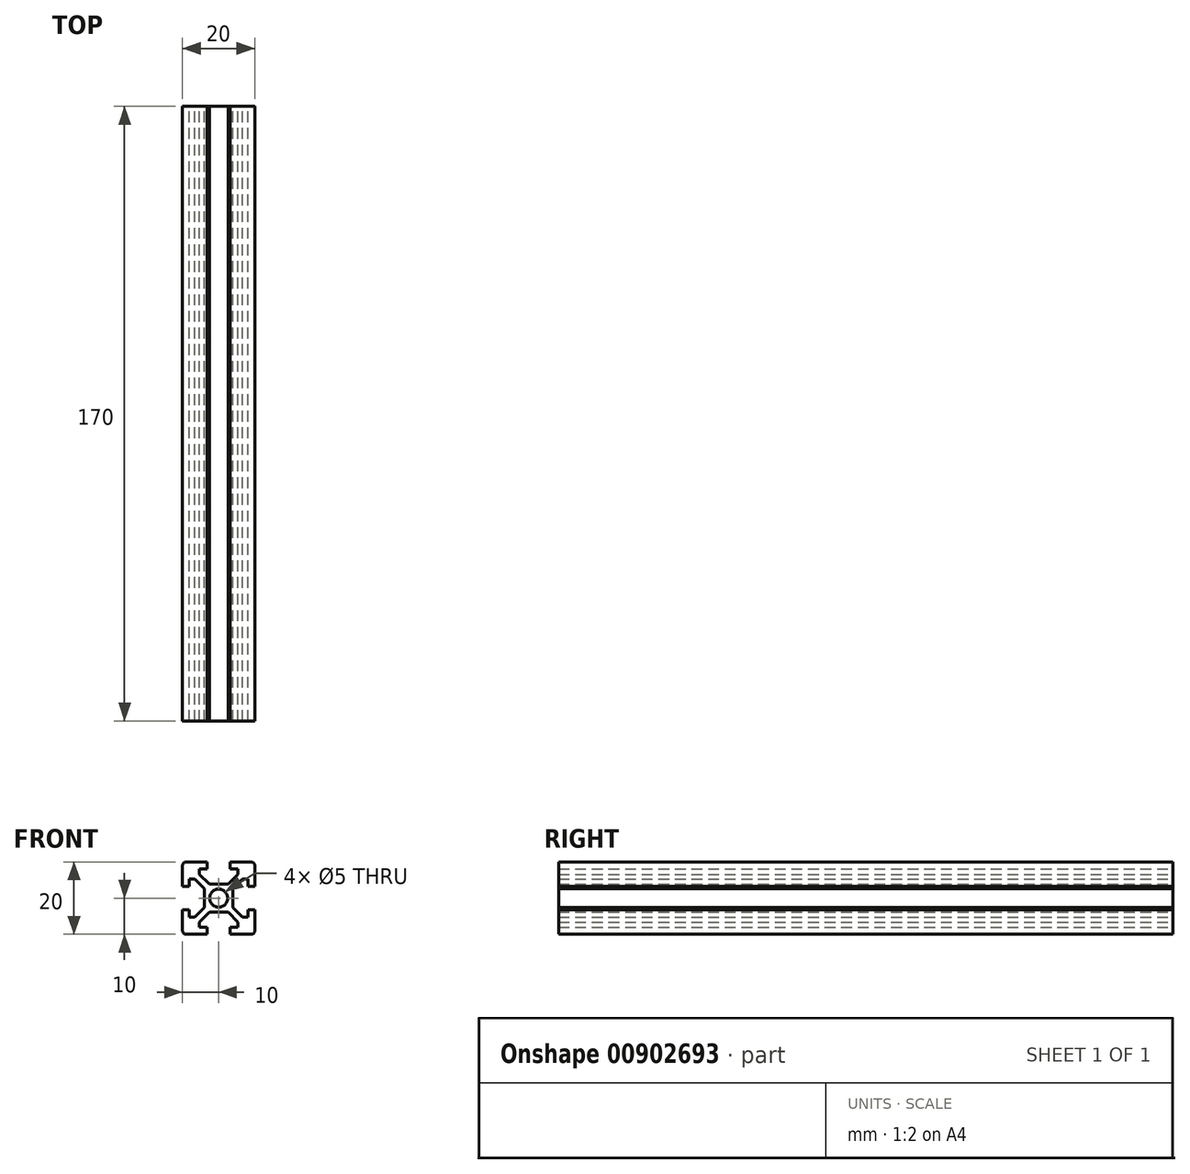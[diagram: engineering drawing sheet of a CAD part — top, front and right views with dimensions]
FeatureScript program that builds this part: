
annotation { "Feature Type Name" : "Feature", "Feature Type Description" : "" }
export const myFeature = defineFeature(function(context is Context, id is Id, definition is map)
    precondition{}
    {
        {
            var Q0;
            Q0=qCreatedBy(makeId("Front.planeOp"),FACE);
            var sketch = newSketch(context, id + "F0", { "sketchPlane" : qUnion([Q0])});
            skLineSegment(sketch, "E0", {"start": v(3.2, 10) * mm, "end": v(9, 10) * mm});
            skLineSegment(sketch, "E1", {"start": v(10, 9) * mm, "end": v(10, 3.2) * mm});
            skLineSegment(sketch, "E2", {"start": v(10, 3.2) * mm, "end": v(8.1, 3.2) * mm});
            skLineSegment(sketch, "E3", {"start": v(8.1, 3.2) * mm, "end": v(8.1, 5.3) * mm});
            skLineSegment(sketch, "E4", {"start": v(8.1, 5.3) * mm, "end": v(6.6, 5.3) * mm});
            skLineSegment(sketch, "E5", {"start": v(5.3, 6.6) * mm, "end": v(5.3, 8.1) * mm});
            skLineSegment(sketch, "E6", {"start": v(5.3, 8.1) * mm, "end": v(3.2, 8.1) * mm});
            skLineSegment(sketch, "E7", {"start": v(3.2, 8.1) * mm, "end": v(3.2, 10) * mm});
            skArc(sketch, "E8", {"start": v(2.5, 0) * mm, "mid": v(1.77, 1.77) * mm, "end": v(0, 2.5) * mm});
            skLineSegment(sketch, "E9", {"start": v(0, 2.5) * mm, "end": v(0, 3.9) * mm});
            skLineSegment(sketch, "E10", {"start": v(0, 3.9) * mm, "end": v(2.6, 3.9) * mm});
            skLineSegment(sketch, "E11", {"start": v(2.6, 3.9) * mm, "end": v(5.3, 6.6) * mm});
            skLineSegment(sketch, "E12", {"start": v(6.6, 5.3) * mm, "end": v(3.9, 2.6) * mm});
            skLineSegment(sketch, "E13", {"start": v(3.9, 2.6) * mm, "end": v(3.9, 0) * mm});
            skLineSegment(sketch, "E14", {"start": v(3.9, 0) * mm, "end": v(2.5, 0) * mm});
            skPoint(sketch, "E15.visualSharp", {"position": v(10, 10) * mm});
            skArc(sketch, "E15.filletArc", {"start": v(10, 9) * mm, "mid": v(9.7, 9.7) * mm, "end": v(9, 10) * mm});
            skArc(sketch, "E16.1.0", {"start": v(0, 2.5) * mm, "mid": v(-1.77, 1.77) * mm, "end": v(-2.5, 0) * mm});
            skLineSegment(sketch, "E16.1.1", {"start": v(-5.3, 8.1) * mm, "end": v(-5.3, 6.6) * mm});
            skLineSegment(sketch, "E16.1.2", {"start": v(-5.3, 6.6) * mm, "end": v(-2.6, 3.9) * mm});
            skLineSegment(sketch, "E16.1.3", {"start": v(0, 3.9) * mm, "end": v(0, 2.5) * mm});
            skLineSegment(sketch, "E16.1.4", {"start": v(-3.2, 8.1) * mm, "end": v(-5.3, 8.1) * mm});
            skLineSegment(sketch, "E16.1.5", {"start": v(-2.6, 3.9) * mm, "end": v(0, 3.9) * mm});
            skLineSegment(sketch, "E16.1.6", {"start": v(-3.2, 10) * mm, "end": v(-3.2, 8.1) * mm});
            skLineSegment(sketch, "E16.1.7", {"start": v(-10, 3.2) * mm, "end": v(-10, 9) * mm});
            skLineSegment(sketch, "E16.1.8", {"start": v(-3.9, 0) * mm, "end": v(-3.9, 2.6) * mm});
            skLineSegment(sketch, "E16.1.9", {"start": v(-3.9, 2.6) * mm, "end": v(-6.6, 5.3) * mm});
            skLineSegment(sketch, "E16.1.10", {"start": v(-2.5, 0) * mm, "end": v(-3.9, 0) * mm});
            skLineSegment(sketch, "E16.1.11", {"start": v(-6.6, 5.3) * mm, "end": v(-8.1, 5.3) * mm});
            skLineSegment(sketch, "E16.1.12", {"start": v(-9, 10) * mm, "end": v(-3.2, 10) * mm});
            skLineSegment(sketch, "E16.1.13", {"start": v(-8.1, 5.3) * mm, "end": v(-8.1, 3.2) * mm});
            skLineSegment(sketch, "E16.1.14", {"start": v(-8.1, 3.2) * mm, "end": v(-10, 3.2) * mm});
            skPoint(sketch, "E16.1.15", {"position": v(-10, 10) * mm});
            skArc(sketch, "E16.1.16", {"start": v(-9, 10) * mm, "mid": v(-9.7, 9.7) * mm, "end": v(-10, 9) * mm});
            skArc(sketch, "E16.2.0", {"start": v(-2.5, 0) * mm, "mid": v(-1.77, -1.77) * mm, "end": v(0, -2.5) * mm});
            skLineSegment(sketch, "E16.2.1", {"start": v(-8.1, -5.3) * mm, "end": v(-6.6, -5.3) * mm});
            skLineSegment(sketch, "E16.2.2", {"start": v(-6.6, -5.3) * mm, "end": v(-3.9, -2.6) * mm});
            skLineSegment(sketch, "E16.2.3", {"start": v(-3.9, 0) * mm, "end": v(-2.5, 0) * mm});
            skLineSegment(sketch, "E16.2.4", {"start": v(-8.1, -3.2) * mm, "end": v(-8.1, -5.3) * mm});
            skLineSegment(sketch, "E16.2.5", {"start": v(-3.9, -2.6) * mm, "end": v(-3.9, 0) * mm});
            skLineSegment(sketch, "E16.2.6", {"start": v(-10, -3.2) * mm, "end": v(-8.1, -3.2) * mm});
            skLineSegment(sketch, "E16.2.7", {"start": v(-3.2, -10) * mm, "end": v(-9, -10) * mm});
            skLineSegment(sketch, "E16.2.8", {"start": v(0, -3.9) * mm, "end": v(-2.6, -3.9) * mm});
            skLineSegment(sketch, "E16.2.9", {"start": v(-2.6, -3.9) * mm, "end": v(-5.3, -6.6) * mm});
            skLineSegment(sketch, "E16.2.10", {"start": v(0, -2.5) * mm, "end": v(0, -3.9) * mm});
            skLineSegment(sketch, "E16.2.11", {"start": v(-5.3, -6.6) * mm, "end": v(-5.3, -8.1) * mm});
            skLineSegment(sketch, "E16.2.12", {"start": v(-10, -9) * mm, "end": v(-10, -3.2) * mm});
            skLineSegment(sketch, "E16.2.13", {"start": v(-5.3, -8.1) * mm, "end": v(-3.2, -8.1) * mm});
            skLineSegment(sketch, "E16.2.14", {"start": v(-3.2, -8.1) * mm, "end": v(-3.2, -10) * mm});
            skPoint(sketch, "E16.2.15", {"position": v(-10, -10) * mm});
            skArc(sketch, "E16.2.16", {"start": v(-10, -9) * mm, "mid": v(-9.7, -9.7) * mm, "end": v(-9, -10) * mm});
            skArc(sketch, "E16.3.0", {"start": v(0, -2.5) * mm, "mid": v(1.77, -1.77) * mm, "end": v(2.5, 0) * mm});
            skLineSegment(sketch, "E16.3.1", {"start": v(5.3, -8.1) * mm, "end": v(5.3, -6.6) * mm});
            skLineSegment(sketch, "E16.3.2", {"start": v(5.3, -6.6) * mm, "end": v(2.6, -3.9) * mm});
            skLineSegment(sketch, "E16.3.3", {"start": v(0, -3.9) * mm, "end": v(0, -2.5) * mm});
            skLineSegment(sketch, "E16.3.4", {"start": v(3.2, -8.1) * mm, "end": v(5.3, -8.1) * mm});
            skLineSegment(sketch, "E16.3.5", {"start": v(2.6, -3.9) * mm, "end": v(0, -3.9) * mm});
            skLineSegment(sketch, "E16.3.6", {"start": v(3.2, -10) * mm, "end": v(3.2, -8.1) * mm});
            skLineSegment(sketch, "E16.3.7", {"start": v(10, -3.2) * mm, "end": v(10, -9) * mm});
            skLineSegment(sketch, "E16.3.8", {"start": v(3.9, 0) * mm, "end": v(3.9, -2.6) * mm});
            skLineSegment(sketch, "E16.3.9", {"start": v(3.9, -2.6) * mm, "end": v(6.6, -5.3) * mm});
            skLineSegment(sketch, "E16.3.10", {"start": v(2.5, 0) * mm, "end": v(3.9, 0) * mm});
            skLineSegment(sketch, "E16.3.11", {"start": v(6.6, -5.3) * mm, "end": v(8.1, -5.3) * mm});
            skLineSegment(sketch, "E16.3.12", {"start": v(9, -10) * mm, "end": v(3.2, -10) * mm});
            skLineSegment(sketch, "E16.3.13", {"start": v(8.1, -5.3) * mm, "end": v(8.1, -3.2) * mm});
            skLineSegment(sketch, "E16.3.14", {"start": v(8.1, -3.2) * mm, "end": v(10, -3.2) * mm});
            skPoint(sketch, "E16.3.15", {"position": v(10, -10) * mm});
            skArc(sketch, "E16.3.16", {"start": v(9, -10) * mm, "mid": v(9.7, -9.7) * mm, "end": v(10, -9) * mm});
            skSolve(sketch);
        }
        {
            var Q0;
            Q0=makeQuery(id+"F0.imprint","IMPRINT",FACE,{"disambiguationData":[TD([[makeQuery(id+"F0.imprint","IMPRINT",EDGE,{"derivedFrom":sQuery(id+"F0.wireOp",EDGE,"E16.1.0")}),-1.0]])]});
            var Q1;
            Q1=makeQuery(id+"F0.imprint","IMPRINT",FACE,{"disambiguationData":[TD([[makeQuery(id+"F0.imprint","IMPRINT",EDGE,{"derivedFrom":sQuery(id+"F0.wireOp",EDGE,"E0")}),-1.0]])]});
            var Q2;
            Q2=makeQuery(id+"F0.imprint","IMPRINT",FACE,{"disambiguationData":[TD([[makeQuery(id+"F0.imprint","IMPRINT",EDGE,{"derivedFrom":sQuery(id+"F0.wireOp",EDGE,"E16.3.0")}),-1.0]])]});
            var Q3;
            Q3=makeQuery(id+"F0.imprint","IMPRINT",FACE,{"disambiguationData":[TD([[makeQuery(id+"F0.imprint","IMPRINT",EDGE,{"derivedFrom":sQuery(id+"F0.wireOp",EDGE,"E16.2.0")}),-1.0]])]});
            extrude(context, id + "F1", {"entities" : qUnion([Q0, Q1, Q2, Q3]), "depth" : 170 * mm, "offsetDistance" : 25 * mm});
        }
    });
